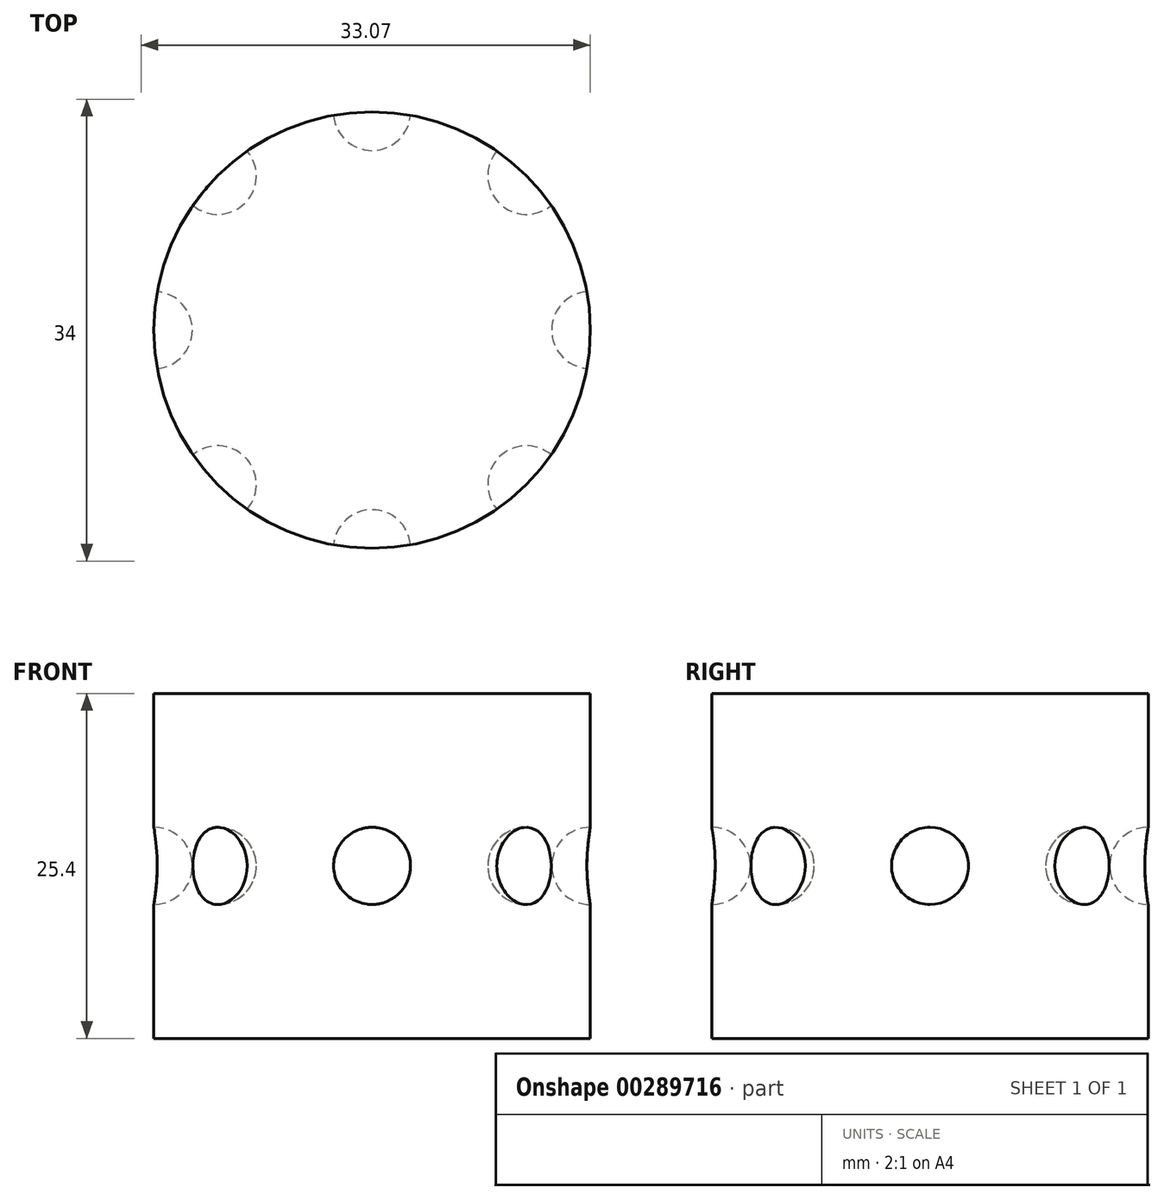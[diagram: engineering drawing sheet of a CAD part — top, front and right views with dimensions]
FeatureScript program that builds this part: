
annotation { "Feature Type Name" : "Feature", "Feature Type Description" : "" }
export const myFeature = defineFeature(function(context is Context, id is Id, definition is map)
    precondition{}
    {
        {
            var Q0;
            Q0=qCreatedBy(makeId("Top.planeOp"),FACE);
            var sketch = newSketch(context, id + "F0", { "sketchPlane" : qUnion([Q0])});
            skCircle(sketch, "E0", {"center": v(0, 0) * mm, "radius": 16.07 * mm});
            skSolve(sketch);
        }
        {
            var Q0;
            Q0 = qSketchRegion(id + "F0", true);
            extrude(context, id + "F1", {"entities" : qUnion([Q0]), "depth" : 25.4 * mm, "symmetric" : true});
        }
        {
            var Q0;
            Q0=qCreatedBy(makeId("Front.planeOp"),FACE);
            var sketch = newSketch(context, id + "F2", { "sketchPlane" : qUnion([Q0])});
            skLineSegment(sketch, "E1", {"start": v(16.07, 12.7) * mm, "end": v(16.07, -12.7) * mm});
            skArc(sketch, "E2", {"start": v(16.07, -2.84) * mm, "mid": v(18.9, 0) * mm, "end": v(16.07, 2.84) * mm});
            skSolve(sketch);
        }
        {
            var Q0;
            Q0 = qSketchRegion(id + "F2", true);
            var Q1;
            Q1=sQuery(id+"F2.wireOp",EDGE,"E1");
            revolve(context, id + "F3", {"entities" : qUnion([Q0]), "axis" : qUnion([Q1]), "revolveType" : RevolveType.FULL});
        }
        {
            var Q0;
            Q0=makeQuery(id+"F3.opRevolve","SWEPT_BODY",BODY,{"disambiguationData":[OSD([sQuery(id+"F2.wireOp",EDGE,"E1"),sQuery(id+"F2.wireOp",EDGE,"E2")])]});
            var Q1;
            Q1=makeQuery(id+"F1.opExtrude","CAP_EDGE",EDGE,{"disambiguationData":[OSD([sQuery(id+"F0.wireOp",EDGE,"E0")])],"isStart":false});
            circularPattern(context, id + "F4", {"operationType" : NewBodyOperationType.REMOVE, "entities" : qUnion([Q0]), "axis" : qUnion([Q1]), "angle" : 360 * degree, "instanceCount" : 8, "equalSpace" : true});
        }
    });
